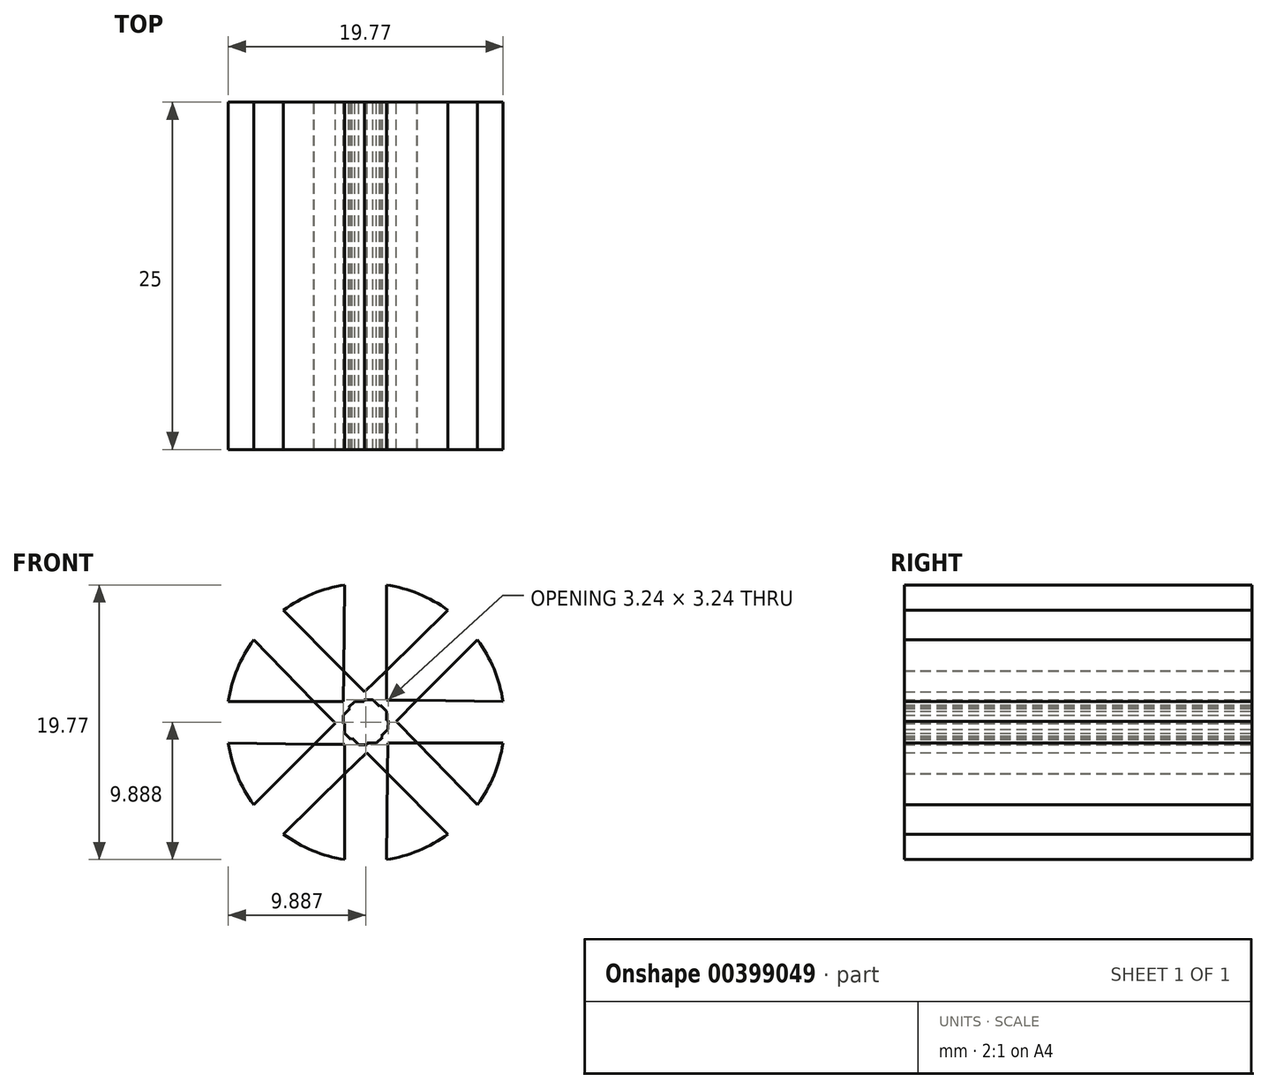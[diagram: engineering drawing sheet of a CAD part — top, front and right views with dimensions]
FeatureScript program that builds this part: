
annotation { "Feature Type Name" : "Feature", "Feature Type Description" : "" }
export const myFeature = defineFeature(function(context is Context, id is Id, definition is map)
    precondition{}
    {
        {
            var Q0;
            Q0=qCreatedBy(makeId("Front.planeOp"),FACE);
            var sketch = newSketch(context, id + "F0", { "sketchPlane" : qUnion([Q0])});
            skLineSegment(sketch, "E0", {"start": v(-1.41, -11.28) * mm, "end": v(1.7, -11.28) * mm});
            skLineSegment(sketch, "E1", {"start": v(1.7, -11.28) * mm, "end": v(1.7, -1.29) * mm});
            skLineSegment(sketch, "E2", {"start": v(-1.41, -11.28) * mm, "end": v(-1.3, -1.29) * mm});
            skArc(sketch, "E3", {"start": v(-1.3, -1.29) * mm, "mid": v(-3.62, -1.93) * mm, "end": v(-5.72, -3.12) * mm});
            skLineSegment(sketch, "E4.1.0", {"start": v(-0.86, -12.4) * mm, "end": v(1.35, -10.2) * mm});
            skLineSegment(sketch, "E4.1.1", {"start": v(-0.86, -12.4) * mm, "end": v(-7.84, -5.24) * mm});
            skLineSegment(sketch, "E4.1.2", {"start": v(1.35, -10.2) * mm, "end": v(-5.72, -3.12) * mm});
            skLineSegment(sketch, "E4.2.0", {"start": v(0.32, -12.8) * mm, "end": v(0.32, -9.67) * mm});
            skLineSegment(sketch, "E4.2.1", {"start": v(0.32, -12.8) * mm, "end": v(-9.68, -12.67) * mm});
            skLineSegment(sketch, "E4.2.2", {"start": v(0.32, -9.67) * mm, "end": v(-9.68, -9.67) * mm});
            skLineSegment(sketch, "E4.3.0", {"start": v(1.43, -12.24) * mm, "end": v(-0.77, -10.03) * mm});
            skLineSegment(sketch, "E4.3.1", {"start": v(1.43, -12.24) * mm, "end": v(-5.72, -19.22) * mm});
            skLineSegment(sketch, "E4.3.2", {"start": v(-0.77, -10.03) * mm, "end": v(-7.84, -17.1) * mm});
            skLineSegment(sketch, "E4.4.0", {"start": v(1.83, -11.06) * mm, "end": v(-1.3, -11.06) * mm});
            skLineSegment(sketch, "E4.4.1", {"start": v(1.83, -11.06) * mm, "end": v(1.7, -21.06) * mm});
            skLineSegment(sketch, "E4.4.2", {"start": v(-1.3, -11.06) * mm, "end": v(-1.3, -21.06) * mm});
            skLineSegment(sketch, "E4.5.0", {"start": v(1.27, -9.95) * mm, "end": v(-0.93, -12.15) * mm});
            skLineSegment(sketch, "E4.5.1", {"start": v(1.27, -9.95) * mm, "end": v(8.26, -17.1) * mm});
            skLineSegment(sketch, "E4.5.2", {"start": v(-0.93, -12.15) * mm, "end": v(6.14, -19.22) * mm});
            skLineSegment(sketch, "E4.6.0", {"start": v(0.1, -9.55) * mm, "end": v(0.1, -12.67) * mm});
            skLineSegment(sketch, "E4.6.1", {"start": v(0.1, -9.55) * mm, "end": v(10.1, -9.67) * mm});
            skLineSegment(sketch, "E4.6.2", {"start": v(0.1, -12.67) * mm, "end": v(10.1, -12.67) * mm});
            skLineSegment(sketch, "E4.7.0", {"start": v(-1.02, -10.1) * mm, "end": v(1.19, -12.31) * mm});
            skLineSegment(sketch, "E4.7.1", {"start": v(-1.02, -10.1) * mm, "end": v(6.14, -3.12) * mm});
            skLineSegment(sketch, "E4.7.2", {"start": v(1.19, -12.31) * mm, "end": v(8.26, -5.24) * mm});
            skArc(sketch, "E5.trimOffspring", {"start": v(-7.84, -5.24) * mm, "mid": v(-9.03, -7.35) * mm, "end": v(-9.68, -9.67) * mm});
            skArc(sketch, "E6.trimOffspring", {"start": v(-9.68, -12.67) * mm, "mid": v(-9.03, -15) * mm, "end": v(-7.84, -17.1) * mm});
            skArc(sketch, "E7.trimOffspring", {"start": v(-5.72, -19.22) * mm, "mid": v(-3.62, -20.41) * mm, "end": v(-1.3, -21.06) * mm});
            skArc(sketch, "E8.trimOffspring", {"start": v(1.7, -21.06) * mm, "mid": v(4.03, -20.41) * mm, "end": v(6.14, -19.22) * mm});
            skArc(sketch, "E9.trimOffspring", {"start": v(8.26, -17.1) * mm, "mid": v(9.45, -15) * mm, "end": v(10.1, -12.67) * mm});
            skArc(sketch, "E10.trimOffspring", {"start": v(10.1, -9.67) * mm, "mid": v(9.45, -7.35) * mm, "end": v(8.26, -5.24) * mm});
            skArc(sketch, "E11.trimOffspring", {"start": v(6.14, -3.12) * mm, "mid": v(4.03, -1.93) * mm, "end": v(1.7, -1.29) * mm});
            skSolve(sketch);
        }
        {
            var Q0;
            Q0 = qSketchRegion(id + "F0", true);
            extrude(context, id + "F1", {"entities" : qUnion([Q0]), "depth" : 25 * mm});
        }
    });
